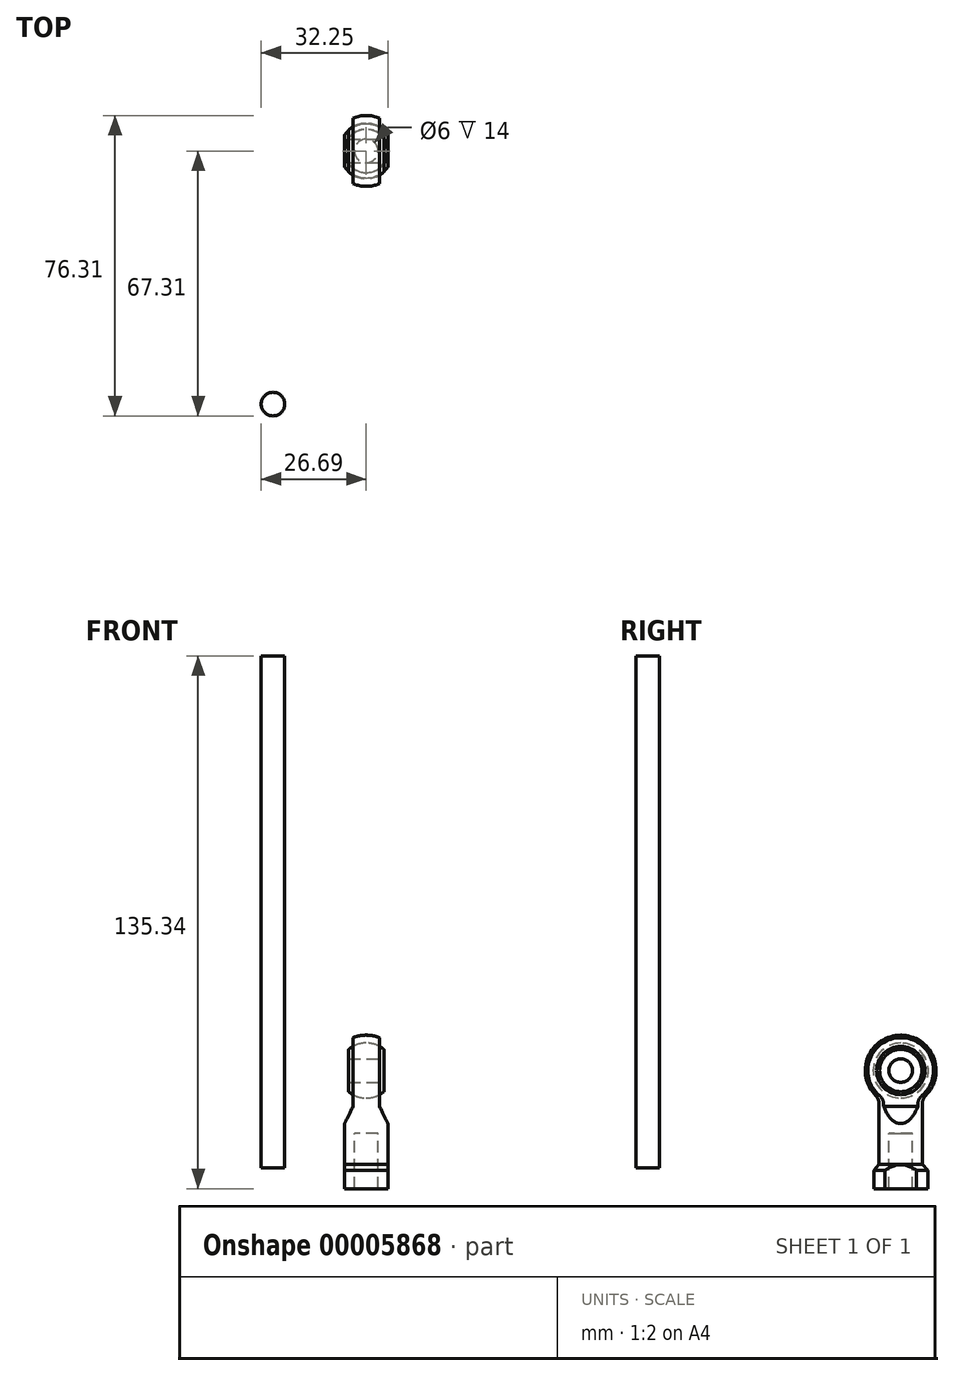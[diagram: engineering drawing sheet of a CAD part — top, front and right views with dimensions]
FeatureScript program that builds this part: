
annotation { "Feature Type Name" : "Feature", "Feature Type Description" : "" }
export const myFeature = defineFeature(function(context is Context, id is Id, definition is map)
    precondition{}
    {
        {
            var Q0;
            Q0=qCreatedBy(makeId("Front.planeOp"),FACE);
            var sketch = newSketch(context, id + "F0", { "sketchPlane" : qUnion([Q0])});
            skLineSegment(sketch, "E0", {"start": v(3, -5.34) * mm, "end": v(6.85, -5.34) * mm});
            skLineSegment(sketch, "E1", {"start": v(6.85, -5.34) * mm, "end": v(6.85, -0.64) * mm});
            skLineSegment(sketch, "E2", {"start": v(6.85, -0.64) * mm, "end": v(5.5, 0.8) * mm});
            skLineSegment(sketch, "E3", {"start": v(5.5, 0.8) * mm, "end": v(5.5, 17.54) * mm});
            skArc(sketch, "E4", {"start": v(5.5, 17.54) * mm, "mid": v(8.52, 27.57) * mm, "end": v(0, 33.66) * mm});
            skLineSegment(sketch, "E5", {"start": v(0, 33.66) * mm, "end": v(0, 8.66) * mm});
            skLineSegment(sketch, "E6", {"start": v(0, 8.66) * mm, "end": v(3, 8.66) * mm});
            skLineSegment(sketch, "E7", {"start": v(3, 8.66) * mm, "end": v(3, -5.34) * mm});
            skPoint(sketch, "E8.orphan", {"position": v(0, -5.34) * mm});
            skSolve(sketch);
        }
        {
            var Q0;
            Q0=makeQuery(id+"F0.imprint","IMPRINT",FACE,{"disambiguationData":[TD([[makeQuery(id+"F0.imprint","IMPRINT",EDGE,{"derivedFrom":sQuery(id+"F0.wireOp",EDGE,"E0")}),1.0]])]});
            var Q1;
            Q1=sQuery(id+"F0.wireOp",EDGE,"E5");
            revolve(context, id + "F1", {"entities" : qUnion([Q0]), "axis" : qUnion([Q1]), "revolveType" : RevolveType.FULL});
        }
        {
            var Q0;
            Q0=qCreatedBy(makeId("Front.planeOp"),FACE);
            var sketch = newSketch(context, id + "F2", { "sketchPlane" : qUnion([Q0])});
            skLineSegment(sketch, "E9", {"start": v(3.38, 34.79) * mm, "end": v(3.38, 15.56) * mm});
            skLineSegment(sketch, "E10", {"start": v(3.38, 15.56) * mm, "end": v(5.56, 11.07) * mm});
            skLineSegment(sketch, "E11", {"start": v(5.56, 11.07) * mm, "end": v(5.56, -7.8) * mm});
            skLineSegment(sketch, "E12", {"start": v(5.56, -7.8) * mm, "end": v(18.45, -7.8) * mm});
            skLineSegment(sketch, "E13", {"start": v(18.45, -7.8) * mm, "end": v(18.45, 34.79) * mm});
            skLineSegment(sketch, "E14", {"start": v(18.45, 34.79) * mm, "end": v(3.37, 34.79) * mm});
            skSolve(sketch);
        }
        {
            var Q0;
            Q0 = qSketchRegion(id + "F2", true);
            extrude(context, id + "F3", {"entities" : qUnion([Q0]), "endBound" : BoundingType.SYMMETRIC, "depth" : 50 * mm});
        }
        {
            var Q0;
            Q0=makeQuery(id+"F3.opExtrude","SWEPT_BODY",BODY,{"disambiguationData":[OSD([sQuery(id+"F2.wireOp",EDGE,"E9"),sQuery(id+"F2.wireOp",EDGE,"E10"),sQuery(id+"F2.wireOp",EDGE,"E11"),sQuery(id+"F2.wireOp",EDGE,"E12"),sQuery(id+"F2.wireOp",EDGE,"E13"),sQuery(id+"F2.wireOp",EDGE,"E14")])]});
            var Q1;
            Q1=qCreatedBy(makeId("Right.planeOp"),FACE);
            mirror(context, id + "F4", {"entities" : qUnion([Q0]), "mirrorPlane" : qUnion([Q1])});
        }
        {
            var Q0;
            Q0=makeQuery(id+"F4.opPattern","COPY",BODY,{"derivedFrom":makeQuery(id+"F3.opExtrude","SWEPT_BODY",BODY,{"disambiguationData":[OSD([sQuery(id+"F2.wireOp",EDGE,"E9"),sQuery(id+"F2.wireOp",EDGE,"E10"),sQuery(id+"F2.wireOp",EDGE,"E11"),sQuery(id+"F2.wireOp",EDGE,"E12"),sQuery(id+"F2.wireOp",EDGE,"E13"),sQuery(id+"F2.wireOp",EDGE,"E14")])]}),"instanceName":"1"});
            var Q1;
            Q1=makeQuery(id+"F3.opExtrude","SWEPT_BODY",BODY,{"disambiguationData":[OSD([sQuery(id+"F2.wireOp",EDGE,"E9"),sQuery(id+"F2.wireOp",EDGE,"E10"),sQuery(id+"F2.wireOp",EDGE,"E11"),sQuery(id+"F2.wireOp",EDGE,"E12"),sQuery(id+"F2.wireOp",EDGE,"E13"),sQuery(id+"F2.wireOp",EDGE,"E14")])]});
            var Q2;
            Q2=makeQuery(id+"F1.opRevolve","SWEPT_BODY",BODY,{"disambiguationData":[OSD([sQuery(id+"F0.wireOp",EDGE,"E0"),sQuery(id+"F0.wireOp",EDGE,"E1"),sQuery(id+"F0.wireOp",EDGE,"E2"),sQuery(id+"F0.wireOp",EDGE,"E3"),sQuery(id+"F0.wireOp",EDGE,"E4"),sQuery(id+"F0.wireOp",EDGE,"E5")])]});
            booleanBodies(context, id + "F5", {"operationType" : BooleanOperationType.SUBTRACTION, "tools" : qUnion([Q0, Q1]), "targets" : qUnion([Q2])});
        }
        {
            var Q0;
            Q0=makeQuery(id+"F5.opBoolean","SPLIT",EDGE,{"disambiguationData":[OD(0.0)],"derivedFrom":makeQuery(id+"F1.opRevolve","SWEPT_EDGE",EDGE,{"disambiguationData":[OSD([sQuery(id+"F0.wireOp",EDGE,"E3"),sQuery(id+"F0.wireOp",EDGE,"E4")])]})});
            var Q1;
            Q1=makeQuery(id+"F5.opBoolean","SPLIT",EDGE,{"disambiguationData":[OD(1.0)],"derivedFrom":makeQuery(id+"F1.opRevolve","SWEPT_EDGE",EDGE,{"disambiguationData":[OSD([sQuery(id+"F0.wireOp",EDGE,"E3"),sQuery(id+"F0.wireOp",EDGE,"E4")])]})});
            fillet(context, id + "F6", {"entities" : qUnion([Q0, Q1]), "radius" : 3 * mm, "tangentPropagation" : true, "allowEdgeOverflow" : false});
        }
        {
            var Q0;
            Q0=qCreatedBy(makeId("Right.planeOp"),FACE);
            var sketch = newSketch(context, id + "F7", { "sketchPlane" : qUnion([Q0])});
            skArc(sketch, "E15.0", {"start": v(5.4, 18.31) * mm, "mid": v(0, 33) * mm, "end": v(-5.4, 18.31) * mm});
            skArc(sketch, "E16", {"start": v(0, 17.66) * mm, "mid": v(7, 24.66) * mm, "end": v(0, 31.66) * mm});
            skLineSegment(sketch, "E17", {"start": v(0, 31.66) * mm, "end": v(0, 17.66) * mm});
            skSolve(sketch);
        }
        {
            var Q0;
            Q0 = qSketchRegion(id + "F7", true);
            var Q1;
            Q1=sQuery(id+"F7.wireOp",EDGE,"E17");
            revolve(context, id + "F8", {"entities" : qUnion([Q0]), "axis" : qUnion([Q1]), "revolveType" : RevolveType.FULL});
        }
        {
            var Q0;
            Q0=makeQuery(id+"F8.opRevolve","SWEPT_BODY",BODY,{"disambiguationData":[OSD([sQuery(id+"F7.wireOp",EDGE,"E16"),sQuery(id+"F7.wireOp",EDGE,"E17")])]});
            transform(context, id + "F9", {"entities" : qUnion([Q0]), "transformType" : TransformType.TRANSLATION_3D, "dx" : 0 * mm, "dy" : 0 * mm, "dz" : 0 * mm, "makeCopy" : true});
        }
        {
            var Q0;
            Q0=makeQuery(id+"F8.opRevolve","SWEPT_BODY",BODY,{"disambiguationData":[OSD([sQuery(id+"F7.wireOp",EDGE,"E16"),sQuery(id+"F7.wireOp",EDGE,"E17")])]});
            var Q1;
            Q1=makeQuery(id+"F1.opRevolve","SWEPT_BODY",BODY,{"disambiguationData":[OSD([sQuery(id+"F0.wireOp",EDGE,"E0"),sQuery(id+"F0.wireOp",EDGE,"E1"),sQuery(id+"F0.wireOp",EDGE,"E2"),sQuery(id+"F0.wireOp",EDGE,"E3"),sQuery(id+"F0.wireOp",EDGE,"E4"),sQuery(id+"F0.wireOp",EDGE,"E5")])]});
            booleanBodies(context, id + "F10", {"operationType" : BooleanOperationType.SUBTRACTION, "tools" : qUnion([Q0]), "targets" : qUnion([Q1])});
        }
        {
            var Q0;
            Q0=qCreatedBy(makeId("Front.planeOp"),FACE);
            var sketch = newSketch(context, id + "F11", { "sketchPlane" : qUnion([Q0])});
            skLineSegment(sketch, "E18.bottom", {"start": v(4.5, 32.4) * mm, "end": v(14.9, 32.4) * mm});
            skLineSegment(sketch, "E18.top", {"start": v(4.5, 17.86) * mm, "end": v(14.9, 17.86) * mm});
            skLineSegment(sketch, "E18.left", {"start": v(4.5, 32.4) * mm, "end": v(4.5, 17.86) * mm});
            skLineSegment(sketch, "E18.right", {"start": v(14.9, 32.4) * mm, "end": v(14.9, 17.86) * mm});
            skSolve(sketch);
        }
        {
            var Q0;
            Q0 = qSketchRegion(id + "F11", true);
            extrude(context, id + "F12", {"entities" : qUnion([Q0]), "endBound" : BoundingType.SYMMETRIC, "depth" : 50 * mm});
        }
        {
            var Q0;
            Q0=makeQuery(id+"F12.opExtrude","SWEPT_BODY",BODY,{"disambiguationData":[OSD([sQuery(id+"F11.wireOp",EDGE,"E18.bottom"),sQuery(id+"F11.wireOp",EDGE,"E18.top"),sQuery(id+"F11.wireOp",EDGE,"E18.left"),sQuery(id+"F11.wireOp",EDGE,"E18.right")])]});
            var Q1;
            Q1=qCreatedBy(makeId("Right.planeOp"),FACE);
            mirror(context, id + "F13", {"entities" : qUnion([Q0]), "mirrorPlane" : qUnion([Q1])});
        }
        {
            var Q0;
            Q0=makeQuery(id+"F13.opPattern","COPY",BODY,{"derivedFrom":makeQuery(id+"F12.opExtrude","SWEPT_BODY",BODY,{"disambiguationData":[OSD([sQuery(id+"F11.wireOp",EDGE,"E18.bottom"),sQuery(id+"F11.wireOp",EDGE,"E18.top"),sQuery(id+"F11.wireOp",EDGE,"E18.left"),sQuery(id+"F11.wireOp",EDGE,"E18.right")])]}),"instanceName":"1"});
            var Q1;
            Q1=makeQuery(id+"F12.opExtrude","SWEPT_BODY",BODY,{"disambiguationData":[OSD([sQuery(id+"F11.wireOp",EDGE,"E18.bottom"),sQuery(id+"F11.wireOp",EDGE,"E18.top"),sQuery(id+"F11.wireOp",EDGE,"E18.left"),sQuery(id+"F11.wireOp",EDGE,"E18.right")])]});
            var Q2;
            Q2=makeQuery(id+"F9.opPattern","COPY",BODY,{"derivedFrom":makeQuery(id+"F8.opRevolve","SWEPT_BODY",BODY,{"disambiguationData":[OSD([sQuery(id+"F7.wireOp",EDGE,"E16"),sQuery(id+"F7.wireOp",EDGE,"E17")])]}),"instanceName":"1"});
            booleanBodies(context, id + "F14", {"operationType" : BooleanOperationType.SUBTRACTION, "tools" : qUnion([Q0, Q1]), "targets" : qUnion([Q2])});
        }
        {
            var Q0;
            Q0=makeQuery(id+"F14.opBoolean","COPY",FACE,{"derivedFrom":makeQuery(id+"F12.opExtrude","SWEPT_FACE",FACE,{"disambiguationData":[OSD([sQuery(id+"F11.wireOp",EDGE,"E18.left")])]})});
            var sketch = newSketch(context, id + "F15", { "sketchPlane" : qUnion([Q0])});
            skCircle(sketch, "E19", {"center": v(0, 24.66) * mm, "radius": 3 * mm});
            skSolve(sketch);
        }
        {
            var Q0;
            Q0=makeQuery(id+"F15.imprint","IMPRINT",FACE,{"disambiguationData":[TD([[makeQuery(id+"F15.imprint","IMPRINT",EDGE,{"derivedFrom":sQuery(id+"F15.wireOp",EDGE,"E19")}),1.0]])]});
            extrude(context, id + "F16", {"entities" : qUnion([Q0]), "operationType" : NewBodyOperationType.REMOVE, "endBound" : BoundingType.THROUGH_ALL, "oppositeDirection" : true, "depth" : 25 * mm});
        }
        {
            var Q0;
            Q0=qCreatedBy(makeId("Top.planeOp"),FACE);
            var sketch = newSketch(context, id + "F17", { "sketchPlane" : qUnion([Q0])});
            skCircle(sketch, "E20", {"center": v(-23.69, -64.31) * mm, "radius": 3 * mm});
            skSolve(sketch);
        }
        {
            var Q0;
            Q0=makeQuery(id+"F17.imprint","IMPRINT",FACE,{"disambiguationData":[TD([[makeQuery(id+"F17.imprint","IMPRINT",EDGE,{"derivedFrom":sQuery(id+"F17.wireOp",EDGE,"E20")}),1.0]])]});
            extrude(context, id + "F18", {"entities" : qUnion([Q0]), "depth" : 130 * mm});
        }
    });
